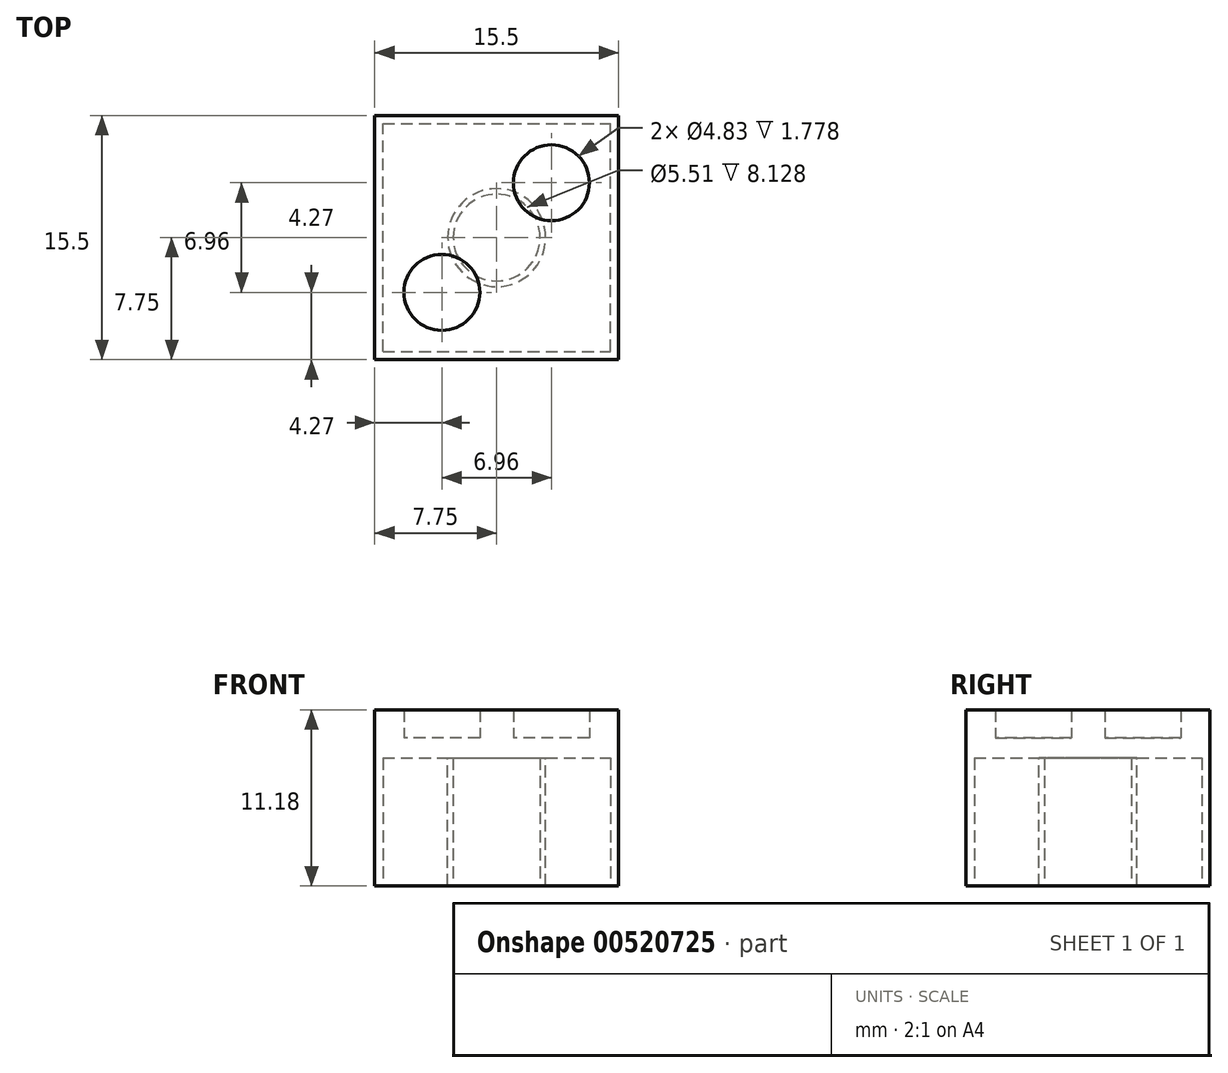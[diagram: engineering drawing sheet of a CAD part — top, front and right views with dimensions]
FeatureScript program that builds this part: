
annotation { "Feature Type Name" : "Feature", "Feature Type Description" : "" }
export const myFeature = defineFeature(function(context is Context, id is Id, definition is map)
    precondition{}
    {
        {
            var Q0;
            Q0=qCreatedBy(makeId("Top.planeOp"),FACE);
            var sketch = newSketch(context, id + "F0", { "sketchPlane" : qUnion([Q0])});
            skLineSegment(sketch, "E0.bottom", {"start": v(-7.75, 7.75) * mm, "end": v(7.75, 7.75) * mm});
            skLineSegment(sketch, "E0.top", {"start": v(-7.75, -7.75) * mm, "end": v(7.75, -7.75) * mm});
            skLineSegment(sketch, "E0.left", {"start": v(-7.75, 7.75) * mm, "end": v(-7.75, -7.75) * mm});
            skLineSegment(sketch, "E0.right", {"start": v(7.75, 7.75) * mm, "end": v(7.75, -7.75) * mm});
            skPoint(sketch, "E0.middle", {"position": v(0, 0) * mm});
            skSolve(sketch);
        }
        {
            var Q0;
            Q0=makeQuery(id+"F0.imprint","IMPRINT",FACE,{"disambiguationData":[TD([[makeQuery(id+"F0.imprint","IMPRINT",EDGE,{"derivedFrom":sQuery(id+"F0.wireOp",EDGE,"E0.bottom")}),-1.0]])]});
            extrude(context, id + "F1", {"entities" : qUnion([Q0]), "depth" : 9.4 * mm, "offsetDistance" : 25.4 * mm});
        }
        {
            var Q0;
            Q0=makeQuery(id+"F1.opExtrude","CAP_FACE",FACE,{"disambiguationData":[OSD([sQuery(id+"F0.wireOp",EDGE,"E0.bottom"),sQuery(id+"F0.wireOp",EDGE,"E0.top"),sQuery(id+"F0.wireOp",EDGE,"E0.left"),sQuery(id+"F0.wireOp",EDGE,"E0.right")])],"isStart":false});
            var sketch = newSketch(context, id + "F2", { "sketchPlane" : qUnion([Q0])});
            skCircle(sketch, "E1", {"center": v(-3.48, 3.48) * mm, "radius": 2.41 * mm});
            skCircle(sketch, "E2.MirrorC", {"center": v(3.48, 3.48) * mm, "radius": 2.41 * mm});
            skCircle(sketch, "E3.MirrorC", {"center": v(-3.48, -3.48) * mm, "radius": 2.41 * mm});
            skCircle(sketch, "E4.MirrorC", {"center": v(3.48, -3.48) * mm, "radius": 2.41 * mm});
            skSolve(sketch);
        }
        {
            var Q0;
            Q0=makeQuery(id+"F2.imprint","IMPRINT",FACE,{"disambiguationData":[TD([[makeQuery(id+"F2.imprint","IMPRINT",EDGE,{"derivedFrom":sQuery(id+"F2.wireOp",EDGE,"E1")}),1.0]])]});
            var Q1;
            Q1=makeQuery(id+"F2.imprint","IMPRINT",FACE,{"disambiguationData":[TD([[makeQuery(id+"F2.imprint","IMPRINT",EDGE,{"derivedFrom":sQuery(id+"F2.wireOp",EDGE,"E2.MirrorC")}),-1.0]])]});
            var Q2;
            Q2=makeQuery(id+"F2.imprint","IMPRINT",FACE,{"disambiguationData":[TD([[makeQuery(id+"F2.imprint","IMPRINT",EDGE,{"derivedFrom":sQuery(id+"F2.wireOp",EDGE,"E4.MirrorC")}),1.0]])]});
            var Q3;
            Q3=makeQuery(id+"F2.imprint","IMPRINT",FACE,{"disambiguationData":[TD([[makeQuery(id+"F2.imprint","IMPRINT",EDGE,{"derivedFrom":sQuery(id+"F2.wireOp",EDGE,"E3.MirrorC")}),-1.0]])]});
            extrude(context, id + "F3", {"entities" : qUnion([Q0, Q1, Q2, Q3]), "operationType" : NewBodyOperationType.ADD, "depth" : 1.78 * mm, "offsetDistance" : 25.4 * mm});
        }
        {
            var Q0;
            Q0=makeQuery(id+"F1.opExtrude","CAP_FACE",FACE,{"disambiguationData":[OSD([sQuery(id+"F0.wireOp",EDGE,"E0.bottom"),sQuery(id+"F0.wireOp",EDGE,"E0.top"),sQuery(id+"F0.wireOp",EDGE,"E0.left"),sQuery(id+"F0.wireOp",EDGE,"E0.right")])],"isStart":true});
            var sketch = newSketch(context, id + "F4", { "sketchPlane" : qUnion([Q0])});
            skLineSegment(sketch, "E5.bottom", {"start": v(-7.23, 7.23) * mm, "end": v(7.23, 7.23) * mm});
            skLineSegment(sketch, "E5.top", {"start": v(-7.23, -7.23) * mm, "end": v(7.23, -7.23) * mm});
            skLineSegment(sketch, "E5.left", {"start": v(-7.23, 7.23) * mm, "end": v(-7.23, -7.23) * mm});
            skLineSegment(sketch, "E5.right", {"start": v(7.23, 7.23) * mm, "end": v(7.23, -7.23) * mm});
            skPoint(sketch, "E5.middle", {"position": v(0, 0) * mm});
            skSolve(sketch);
        }
        {
            var Q0;
            Q0=makeQuery(id+"F4.imprint","IMPRINT",FACE,{"disambiguationData":[TD([[makeQuery(id+"F4.imprint","IMPRINT",EDGE,{"derivedFrom":sQuery(id+"F4.wireOp",EDGE,"E5.bottom")}),-1.0]])]});
            extrude(context, id + "F5", {"entities" : qUnion([Q0]), "operationType" : NewBodyOperationType.REMOVE, "oppositeDirection" : true, "depth" : 8.13 * mm, "offsetDistance" : 25.4 * mm});
        }
        {
            var Q0;
            Q0=makeQuery(id+"F5.boolean.opBoolean","COPY",FACE,{"derivedFrom":makeQuery(id+"F5.opExtrude","CAP_FACE",FACE,{"disambiguationData":[OSD([sQuery(id+"F4.wireOp",EDGE,"E5.bottom"),sQuery(id+"F4.wireOp",EDGE,"E5.top"),sQuery(id+"F4.wireOp",EDGE,"E5.left"),sQuery(id+"F4.wireOp",EDGE,"E5.right")])],"isStart":false})});
            var sketch = newSketch(context, id + "F6", { "sketchPlane" : qUnion([Q0])});
            skCircle(sketch, "E6", {"center": v(0, 0) * mm, "radius": 3.11 * mm});
            skSolve(sketch);
        }
        {
            var Q0;
            Q0=makeQuery(id+"F6.imprint","IMPRINT",FACE,{"disambiguationData":[TD([[makeQuery(id+"F6.imprint","IMPRINT",EDGE,{"derivedFrom":sQuery(id+"F6.wireOp",EDGE,"E6")}),1.0]])]});
            extrude(context, id + "F7", {"entities" : qUnion([Q0]), "operationType" : NewBodyOperationType.ADD, "depth" : 8.13 * mm, "offsetDistance" : 25.4 * mm});
        }
        {
            var Q0;
            Q0=makeQuery(id+"F7.opExtrude","CAP_FACE",FACE,{"disambiguationData":[OSD([sQuery(id+"F6.wireOp",EDGE,"E6")])],"isStart":false});
            var sketch = newSketch(context, id + "F8", { "sketchPlane" : qUnion([Q0])});
            skCircle(sketch, "E7", {"center": v(0, 0) * mm, "radius": 2.76 * mm});
            skSolve(sketch);
        }
        {
            var Q0;
            Q0=makeQuery(id+"F8.imprint","IMPRINT",FACE,{"disambiguationData":[TD([[makeQuery(id+"F8.imprint","IMPRINT",EDGE,{"derivedFrom":sQuery(id+"F8.wireOp",EDGE,"E7")}),1.0]])]});
            extrude(context, id + "F9", {"entities" : qUnion([Q0]), "operationType" : NewBodyOperationType.REMOVE, "oppositeDirection" : true, "depth" : 8.13 * mm, "offsetDistance" : 25.4 * mm});
        }
    });
